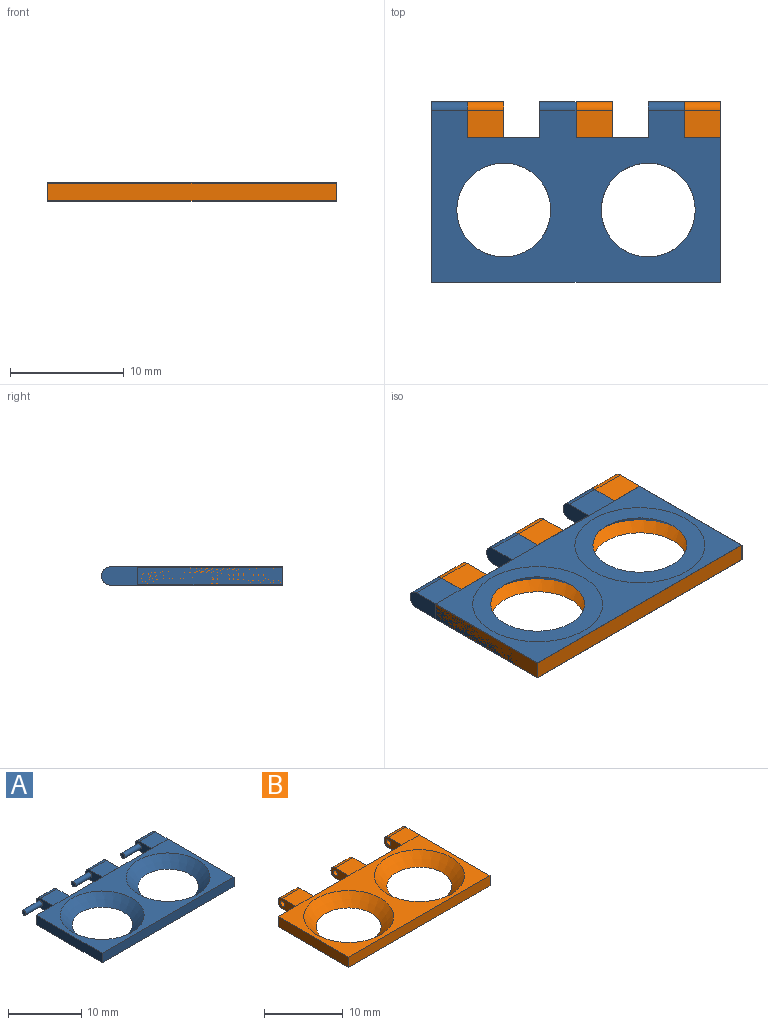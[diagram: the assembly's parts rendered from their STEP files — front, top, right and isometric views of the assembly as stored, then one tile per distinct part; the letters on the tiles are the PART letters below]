
ASSEMBLY  parts=2 mates=1
PART A: 36 faces, bbox 25.4x15.9x1.6 mm
  f0: plane 6.35x1.59mm, normal (0,1,0), area 10.1mm2, adj f3,f5,f16,f22
  f1: plane 6.35x1.59mm, normal (0,1,0), area 10.1mm2, adj f3,f5,f12,f17
  f2: plane 15.88x1.6mm, normal (1,0,0), area 25mm2, adj f3,f5,f6,f10,f11,f13,f24,f25
  f3: plane 25.4x12.7mm, normal (0,0,1), area 117.4mm2, adj f0,f1,f2,f4,f6,f7,f8,f9
  f4: plane 12.7x1.59mm, normal (-1,0,0), area 20.2mm2, adj f3,f5,f6,f7
  f5: plane 25.4x15.11mm, normal (0,0,-1), area 238.5mm2, adj f0,f1,f2,f4,f6,f7,f8,f9
  f6: plane 25.4x1.59mm, normal (0,-1,0), area 40.3mm2, adj f2,f3,f4,f5
  f7: plane 3.18x1.59mm, normal (0,1,0), area 5mm2, adj f3,f4,f5,f21
  f8: cone r=3.17mm half-angle=45deg, axis (0,0,1), area 69.4mm2, adj f3,f5
  f9: cone r=3.17mm half-angle=45deg, axis (0,0,1), area 69.4mm2, adj f3,f5
  f10: plane 3.18x0.01mm, normal (0,-1,0), area 0mm2, adj f2,f3,f11,f12
  f11: plane 3.18x2.41mm, normal (0,0,1), area 7.7mm2, adj f2,f10,f12,f24
  f12: plane 3.18x1.6mm, normal (-1,0,0), area 4.3mm2, adj f1,f5,f10,f11,f13,f24,f25,f32
  f13: plane 3.18x0.08mm, normal (0,1,0), area 0.2mm2, adj f2,f12,f24,f25
  f14: plane 3.18x0.01mm, normal (0,-1,0), area 0mm2, adj f3,f15,f16,f17
  f15: plane 3.18x2.41mm, normal (0,0,1), area 7.7mm2, adj f14,f16,f17,f26
  f16: plane 3.18x1.6mm, normal (-1,0,0), area 4.3mm2, adj f0,f5,f14,f15,f18,f26,f27,f34
  f17: plane 3.18x1.6mm, normal (1,0,0), area 4.8mm2, adj f1,f5,f14,f15,f18,f26,f27
  f18: plane 3.18x0.08mm, normal (0,1,0), area 0.2mm2, adj f16,f17,f26,f27
  f19: plane 3.18x0.01mm, normal (0,-1,0), area 0mm2, adj f3,f20,f21,f22
  f20: plane 3.18x2.41mm, normal (0,0,1), area 7.7mm2, adj f19,f21,f22,f28
  f21: plane 3.18x1.6mm, normal (-1,0,0), area 4.3mm2, adj f5,f7,f19,f20,f23,f28,f29,f30
  f22: plane 3.18x1.6mm, normal (1,0,0), area 4.8mm2, adj f0,f5,f19,f20,f23,f28,f29
  f23: plane 3.18x0.08mm, normal (0,1,0), area 0.2mm2, adj f21,f22,f28,f29
  f24: cylinder r=0.76mm len=3.18mm, axis (1,0,0), area 3.8mm2, adj f2,f11,f12,f13
  f25: cylinder r=0.76mm len=3.18mm, axis (1,0,0), area 3.8mm2, adj f2,f5,f12,f13
  f26: cylinder r=0.76mm len=3.18mm, axis (1,0,0), area 3.8mm2, adj f15,f16,f17,f18
  f27: cylinder r=0.76mm len=3.18mm, axis (1,0,0), area 3.8mm2, adj f5,f16,f17,f18
  f28: cylinder r=0.76mm len=3.18mm, axis (1,0,0), area 3.8mm2, adj f20,f21,f22,f23
  f29: cylinder r=0.76mm len=3.18mm, axis (1,0,0), area 3.8mm2, adj f5,f21,f22,f23
  f30: cylinder r=0.4mm len=3.18mm, axis (1,0,0), area 7.9mm2, adj f21,f31
  f31: plane 0.79x0.79mm, normal (-1,0,0), area 0.5mm2, adj f30
  f32: cylinder r=0.4mm len=3.18mm, axis (1,0,0), area 7.9mm2, adj f12,f33
  f33: plane 0.79x0.79mm, normal (-1,0,0), area 0.5mm2, adj f32
  f34: cylinder r=0.4mm len=3.18mm, axis (1,0,0), area 7.9mm2, adj f16,f35
  f35: plane 0.79x0.79mm, normal (-1,0,0), area 0.5mm2, adj f34
PART B: 33 faces, bbox 25.4x15.9x1.6 mm
  f0: plane 6.35x1.59mm, normal (0,1,0), area 10.1mm2, adj f3,f5,f16,f22
  f1: plane 6.35x1.59mm, normal (0,1,0), area 10.1mm2, adj f3,f5,f12,f17
  f2: plane 15.88x1.6mm, normal (1,0,0), area 24.5mm2, adj f3,f5,f6,f10,f11,f13,f24,f25
  f3: plane 25.4x12.7mm, normal (0,0,1), area 117.4mm2, adj f0,f1,f2,f4,f6,f7,f8,f9
  f4: plane 12.7x1.59mm, normal (-1,0,0), area 20.2mm2, adj f3,f5,f6,f7
  f5: plane 25.4x15.11mm, normal (0,0,-1), area 238.5mm2, adj f0,f1,f2,f4,f6,f7,f8,f9
  f6: plane 25.4x1.59mm, normal (0,-1,0), area 40.3mm2, adj f2,f3,f4,f5
  f7: plane 3.18x1.59mm, normal (0,1,0), area 5mm2, adj f3,f4,f5,f21
  f8: cone r=3.17mm half-angle=45deg, axis (0,0,1), area 69.4mm2, adj f3,f5
  f9: cone r=3.17mm half-angle=45deg, axis (0,0,1), area 69.4mm2, adj f3,f5
  f10: plane 3.18x0.01mm, normal (0,-1,0), area 0mm2, adj f2,f3,f11,f12
  f11: plane 3.18x2.41mm, normal (0,0,1), area 7.7mm2, adj f2,f10,f12,f24
  f12: plane 3.18x1.6mm, normal (-1,0,0), area 4.3mm2, adj f1,f5,f10,f11,f13,f24,f25,f31
  f13: plane 3.18x0.08mm, normal (0,1,0), area 0.2mm2, adj f2,f12,f24,f25
  f14: plane 3.18x0.01mm, normal (0,-1,0), area 0mm2, adj f3,f15,f16,f17
  f15: plane 3.18x2.41mm, normal (0,0,1), area 7.7mm2, adj f14,f16,f17,f26
  f16: plane 3.18x1.6mm, normal (-1,0,0), area 4.3mm2, adj f0,f5,f14,f15,f18,f26,f27,f32
  f17: plane 3.18x1.6mm, normal (1,0,0), area 4.3mm2, adj f1,f5,f14,f15,f18,f26,f27,f32
  f18: plane 3.18x0.08mm, normal (0,1,0), area 0.2mm2, adj f16,f17,f26,f27
  f19: plane 3.18x0.01mm, normal (0,-1,0), area 0mm2, adj f3,f20,f21,f22
  f20: plane 3.18x2.41mm, normal (0,0,1), area 7.7mm2, adj f19,f21,f22,f28
  f21: plane 3.18x1.6mm, normal (-1,0,0), area 4.3mm2, adj f5,f7,f19,f20,f23,f28,f29,f30
  f22: plane 3.18x1.6mm, normal (1,0,0), area 4.3mm2, adj f0,f5,f19,f20,f23,f28,f29,f30
  f23: plane 3.18x0.08mm, normal (0,1,0), area 0.2mm2, adj f21,f22,f28,f29
  f24: cylinder r=0.76mm len=3.18mm, axis (1,0,0), area 3.8mm2, adj f2,f11,f12,f13
  f25: cylinder r=0.76mm len=3.18mm, axis (1,0,0), area 3.8mm2, adj f2,f5,f12,f13
  f26: cylinder r=0.76mm len=3.18mm, axis (1,0,0), area 3.8mm2, adj f15,f16,f17,f18
  f27: cylinder r=0.76mm len=3.18mm, axis (1,0,0), area 3.8mm2, adj f5,f16,f17,f18
  f28: cylinder r=0.76mm len=3.18mm, axis (1,0,0), area 3.8mm2, adj f20,f21,f22,f23
  f29: cylinder r=0.76mm len=3.18mm, axis (1,0,0), area 3.8mm2, adj f5,f21,f22,f23
  f30: cylinder r=0.4mm len=3.18mm, axis (-1,0,0), area 7.9mm2, adj f21,f22
  f31: cylinder r=0.4mm len=3.18mm, axis (-1,0,0), area 7.9mm2, adj f2,f12
  f32: cylinder r=0.4mm len=3.18mm, axis (-1,0,0), area 7.9mm2, adj f16,f17
PLACE A rot(axis=(0,1,0),180deg) t=(-32.29,-38.94,-16.36)mm
PLACE B t=(-32.29,-38.94,-16.37)mm
MATE revolute A.f32 <-> B.f30  axis (1,0,0) through (-38.64,-36.57,-16.36)mm
